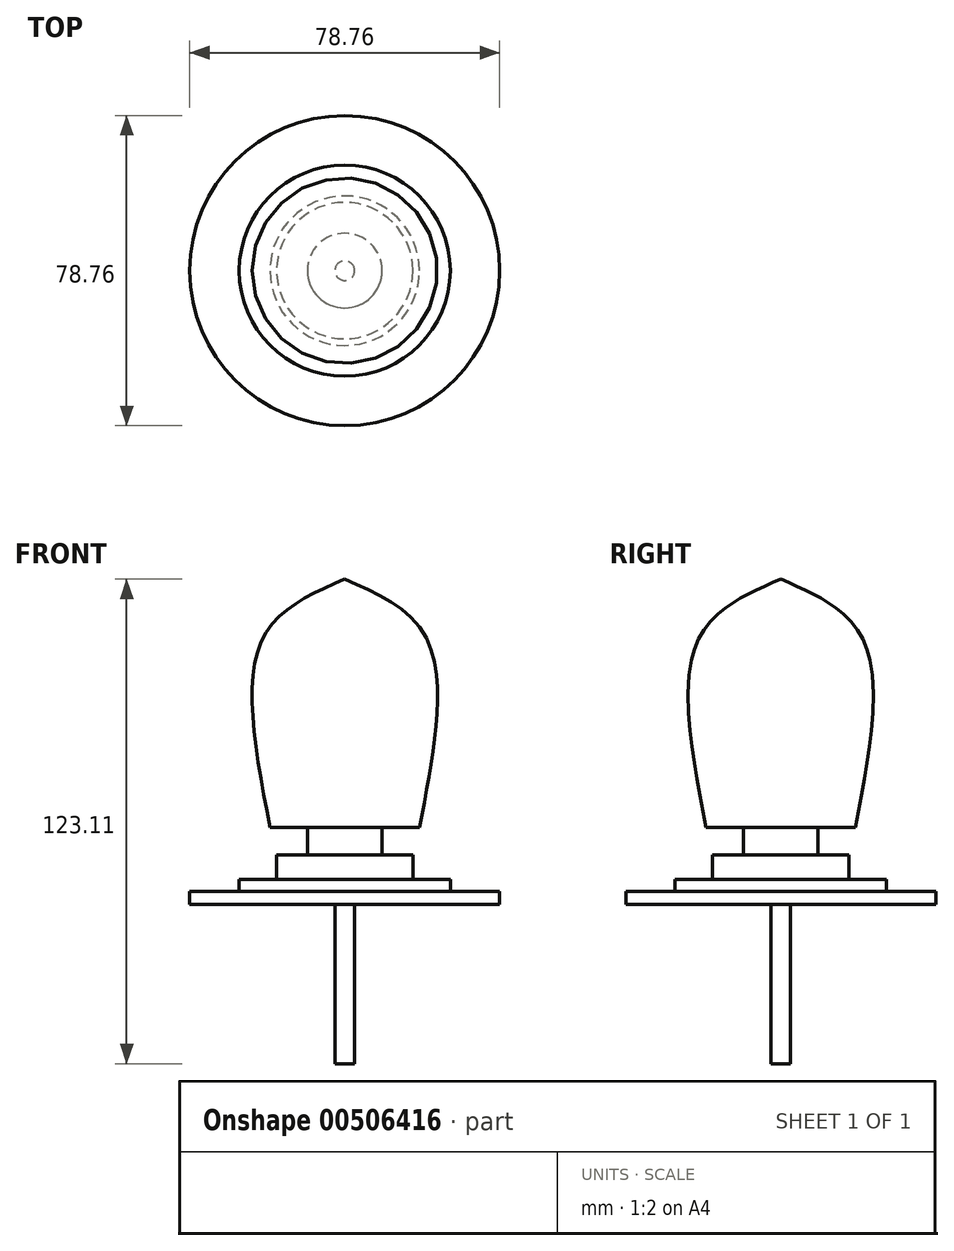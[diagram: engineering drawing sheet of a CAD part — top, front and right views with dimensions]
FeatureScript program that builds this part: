
annotation { "Feature Type Name" : "Feature", "Feature Type Description" : "" }
export const myFeature = defineFeature(function(context is Context, id is Id, definition is map)
    precondition{}
    {
        {
            var Q0;
            Q0=qCreatedBy(makeId("Top.planeOp"),FACE);
            var sketch = newSketch(context, id + "F0", { "sketchPlane" : qUnion([Q0])});
            skCircle(sketch, "E0", {"center": v(0, 0) * mm, "radius": 2.5 * mm});
            skSolve(sketch);
        }
        {
            var Q0;
            Q0=makeQuery(id+"F0.imprint","IMPRINT",FACE,{"disambiguationData":[TD([[makeQuery(id+"F0.imprint","IMPRINT",EDGE,{"derivedFrom":sQuery(id+"F0.wireOp",EDGE,"E0")}),1.0]])]});
            extrude(context, id + "F1", {"entities" : qUnion([Q0]), "endBound" : BoundingType.SYMMETRIC, "depth" : 120 * mm});
        }
        {
            var Q0;
            Q0=qCreatedBy(makeId("Front.planeOp"),FACE);
            var sketch = newSketch(context, id + "F2", { "sketchPlane" : qUnion([Q0])});
            skFitSpline(sketch, "E1", {"points": [v(0, 63.11) * mm, v(-20.94, 47.75) * mm, v(-18.99, 0) * mm], "startDerivative": vector(-60.55, -26.27) * mm, "endDerivative": vector(18.58, -96.41) * mm});
            skLineSegment(sketch, "E2", {"start": v(-18.99, 0) * mm, "end": v(0, 0) * mm});
            skLineSegment(sketch, "E3", {"start": v(0, 0) * mm, "end": v(0, 63.11) * mm});
            skSolve(sketch);
        }
        {
            var Q0;
            Q0=makeQuery(id+"F2.imprint","IMPRINT",FACE,{"disambiguationData":[TD([[makeQuery(id+"F2.imprint","IMPRINT",EDGE,{"derivedFrom":sQuery(id+"F2.wireOp",EDGE,"E1")}),1.0]])]});
            var Q1;
            Q1=sQuery(id+"F2.wireOp",EDGE,"E3");
            revolve(context, id + "F3", {"operationType" : NewBodyOperationType.ADD, "entities" : qUnion([Q0]), "axis" : qUnion([Q1]), "revolveType" : RevolveType.FULL});
        }
        {
            var Q0;
            Q0=qCreatedBy(makeId("Front.planeOp"),FACE);
            var sketch = newSketch(context, id + "F4", { "sketchPlane" : qUnion([Q0])});
            skLineSegment(sketch, "E4", {"start": v(0, 0) * mm, "end": v(9.5, 0) * mm});
            skLineSegment(sketch, "E5", {"start": v(9.5, 0) * mm, "end": v(9.5, -6.98) * mm});
            skLineSegment(sketch, "E6", {"start": v(9.5, -6.98) * mm, "end": v(17.31, -6.98) * mm});
            skLineSegment(sketch, "E7", {"start": v(17.31, -6.98) * mm, "end": v(17.31, -13.13) * mm});
            skLineSegment(sketch, "E8", {"start": v(17.31, -13.13) * mm, "end": v(26.8, -13.13) * mm});
            skLineSegment(sketch, "E9", {"start": v(26.8, -13.13) * mm, "end": v(26.8, -16.2) * mm});
            skLineSegment(sketch, "E10", {"start": v(26.8, -16.2) * mm, "end": v(39.38, -16.2) * mm});
            skLineSegment(sketch, "E11", {"start": v(39.38, -16.2) * mm, "end": v(39.38, -19.55) * mm});
            skLineSegment(sketch, "E12", {"start": v(39.38, -19.55) * mm, "end": v(0, -19.55) * mm});
            skLineSegment(sketch, "E13", {"start": v(0, -19.55) * mm, "end": v(0, 0) * mm});
            skSolve(sketch);
        }
        {
            var Q0;
            Q0=makeQuery(id+"F4.imprint","IMPRINT",FACE,{"disambiguationData":[TD([[makeQuery(id+"F4.imprint","IMPRINT",EDGE,{"derivedFrom":sQuery(id+"F4.wireOp",EDGE,"E4")}),-1.0]])]});
            var Q1;
            Q1=sQuery(id+"F4.wireOp",EDGE,"E13");
            revolve(context, id + "F5", {"operationType" : NewBodyOperationType.ADD, "entities" : qUnion([Q0]), "axis" : qUnion([Q1]), "revolveType" : RevolveType.FULL});
        }
    });
